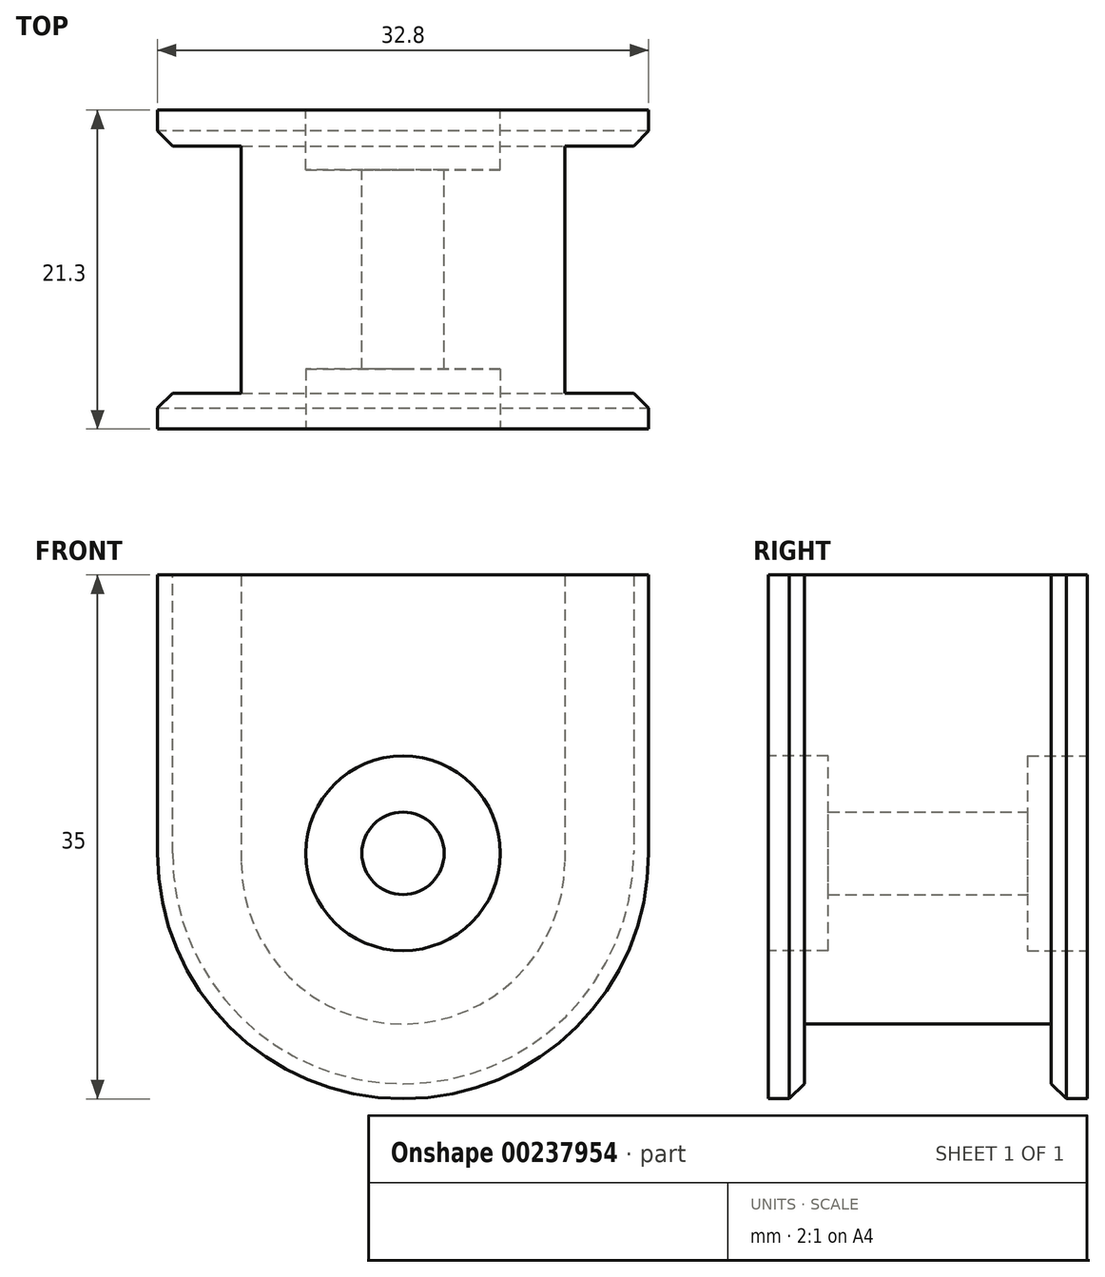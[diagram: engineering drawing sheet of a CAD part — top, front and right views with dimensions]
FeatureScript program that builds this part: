
annotation { "Feature Type Name" : "Feature", "Feature Type Description" : "" }
export const myFeature = defineFeature(function(context is Context, id is Id, definition is map)
    precondition{}
    {
        {
            var Q0;
            Q0=qCreatedBy(makeId("Front.planeOp"),FACE);
            var sketch = newSketch(context, id + "F0", { "sketchPlane" : qUnion([Q0])});
            skLineSegment(sketch, "E0", {"start": v(-10.8, 5) * mm, "end": v(-10.8, -14.2) * mm});
            skLineSegment(sketch, "E1", {"start": v(10.8, 5) * mm, "end": v(10.8, -14.2) * mm});
            skLineSegment(sketch, "E2", {"start": v(-10.8, 5) * mm, "end": v(10.8, 5) * mm});
            skArc(sketch, "E3", {"start": v(-10.8, -14.2) * mm, "mid": v(0, -25) * mm, "end": v(10.8, -14.2) * mm});
            skSolve(sketch);
        }
        {
            var Q0;
            Q0 = qSketchRegion(id + "F0", true);
            extrude(context, id + "F1", {"entities" : qUnion([Q0]), "depth" : 16.5 * mm});
        }
        {
            var Q0;
            Q0=makeQuery(id+"F1.opExtrude","CAP_FACE",FACE,{"disambiguationData":[OSD([sQuery(id+"F0.wireOp",EDGE,"E0"),sQuery(id+"F0.wireOp",EDGE,"E1"),sQuery(id+"F0.wireOp",EDGE,"E2"),sQuery(id+"F0.wireOp",EDGE,"E3")])],"isStart":false});
            var sketch = newSketch(context, id + "F2", { "sketchPlane" : qUnion([Q0])});
            skLineSegment(sketch, "E4.0.0", {"start": v(10.8, -14.2) * mm, "end": v(10.8, 5) * mm});
            skLineSegment(sketch, "E4.0.1", {"start": v(10.8, 5) * mm, "end": v(-10.8, 5) * mm});
            skLineSegment(sketch, "E4.0.2", {"start": v(-10.8, 5) * mm, "end": v(-10.8, -14.2) * mm});
            skArc(sketch, "E4.0.3", {"start": v(-10.8, -14.2) * mm, "mid": v(0, -25) * mm, "end": v(10.8, -14.2) * mm});
            skLineSegment(sketch, "E5.1", {"start": v(16.4, -13.6) * mm, "end": v(16.4, 5) * mm});
            skArc(sketch, "E5.2", {"start": v(-16.4, -13.6) * mm, "mid": v(0, -30) * mm, "end": v(16.4, -13.6) * mm});
            skLineSegment(sketch, "E5.3", {"start": v(-16.4, 5) * mm, "end": v(-16.4, -13.6) * mm});
            skLineSegment(sketch, "E6", {"start": v(-16.4, 5) * mm, "end": v(16.4, 5) * mm});
            skSolve(sketch);
        }
        {
            var Q0;
            Q0=makeQuery(id+"F2.imprint","IMPRINT",FACE,{"disambiguationData":[TD([[makeQuery(id+"F2.imprint","IMPRINT",EDGE,{"derivedFrom":sQuery(id+"F2.wireOp",EDGE,"E4.0.0")}),-1.0]])]});
            var Q1;
            Q1=makeQuery(id+"F2.imprint","IMPRINT",FACE,{"disambiguationData":[TD([[makeQuery(id+"F2.imprint","IMPRINT",EDGE,{"derivedFrom":sQuery(id+"F2.wireOp",EDGE,"E4.0.0")}),1.0]])]});
            extrude(context, id + "F3", {"entities" : qUnion([Q0, Q1]), "operationType" : NewBodyOperationType.ADD, "depth" : 2.4 * mm});
        }
        {
            var Q0;
            Q0=makeQuery(id+"F1.opExtrude","CAP_FACE",FACE,{"disambiguationData":[OSD([sQuery(id+"F0.wireOp",EDGE,"E0"),sQuery(id+"F0.wireOp",EDGE,"E1"),sQuery(id+"F0.wireOp",EDGE,"E2"),sQuery(id+"F0.wireOp",EDGE,"E3")])],"isStart":true});
            var sketch = newSketch(context, id + "F4", { "sketchPlane" : qUnion([Q0])});
            skLineSegment(sketch, "E7.0", {"start": v(-16.4, 5) * mm, "end": v(16.4, 5) * mm});
            skLineSegment(sketch, "E8.0", {"start": v(-16.4, -13.6) * mm, "end": v(-16.4, 5) * mm});
            skArc(sketch, "E9.0", {"start": v(16.4, -13.6) * mm, "mid": v(0, -30) * mm, "end": v(-16.4, -13.6) * mm});
            skLineSegment(sketch, "E10.0", {"start": v(16.4, 5) * mm, "end": v(16.4, -13.6) * mm});
            skSolve(sketch);
        }
        {
            var Q0;
            Q0 = qSketchRegion(id + "F4", true);
            extrude(context, id + "F5", {"entities" : qUnion([Q0]), "operationType" : NewBodyOperationType.ADD, "depth" : 2.4 * mm});
        }
        {
            var Q0;
            Q0=makeQuery(id+"F5.opExtrude","CAP_FACE",FACE,{"disambiguationData":[OSD([sQuery(id+"F4.wireOp",EDGE,"E7.0"),sQuery(id+"F4.wireOp",EDGE,"E8.0"),sQuery(id+"F4.wireOp",EDGE,"E9.0"),sQuery(id+"F4.wireOp",EDGE,"E10.0")])],"isStart":false});
            var sketch = newSketch(context, id + "F6", { "sketchPlane" : qUnion([Q0])});
            skArc(sketch, "E11.0", {"start": v(16.4, -13.6) * mm, "mid": v(0, -30) * mm, "end": v(-16.4, -13.6) * mm, "construction": true});
            skCircle(sketch, "E12", {"center": v(0, -13.6) * mm, "radius": 2.75 * mm});
            skSolve(sketch);
        }
        {
            var Q0;
            Q0 = qSketchRegion(id + "F6", true);
            extrude(context, id + "F7", {"entities" : qUnion([Q0]), "operationType" : NewBodyOperationType.REMOVE, "endBound" : BoundingType.THROUGH_ALL, "oppositeDirection" : true, "depth" : 25 * mm});
        }
        {
            var Q0;
            Q0=makeQuery(id+"F3.opExtrude","CAP_EDGE",EDGE,{"disambiguationData":[OSD([sQuery(id+"F2.wireOp",EDGE,"E5.2")])],"isStart":true});
            var Q1;
            Q1=makeQuery(id+"F5.opExtrude","CAP_EDGE",EDGE,{"disambiguationData":[OSD([sQuery(id+"F4.wireOp",EDGE,"E9.0")])],"isStart":true});
            chamfer(context, id + "F8", {"entities" : qUnion([Q0, Q1]), "width" : 1 * mm, "tangentPropagation" : true});
        }
        {
            var Q0;
            Q0=makeQuery(id+"F5.opExtrude","CAP_FACE",FACE,{"disambiguationData":[OSD([sQuery(id+"F4.wireOp",EDGE,"E7.0"),sQuery(id+"F4.wireOp",EDGE,"E8.0"),sQuery(id+"F4.wireOp",EDGE,"E9.0"),sQuery(id+"F4.wireOp",EDGE,"E10.0")])],"isStart":false});
            var sketch = newSketch(context, id + "F9", { "sketchPlane" : qUnion([Q0])});
            skCircle(sketch, "E13.0", {"center": v(0, -13.6) * mm, "radius": 2.75 * mm, "construction": true});
            skCircle(sketch, "E14", {"center": v(0, -13.6) * mm, "radius": 6.5 * mm});
            skSolve(sketch);
        }
        {
            var Q0;
            Q0 = qSketchRegion(id + "F9", true);
            extrude(context, id + "F10", {"entities" : qUnion([Q0]), "operationType" : NewBodyOperationType.REMOVE, "oppositeDirection" : true, "depth" : 4 * mm});
        }
        {
            var Q0;
            Q0=makeQuery(id+"F3.opExtrude","CAP_FACE",FACE,{"disambiguationData":[OSD([sQuery(id+"F2.wireOp",EDGE,"E5.1"),sQuery(id+"F2.wireOp",EDGE,"E5.2"),sQuery(id+"F2.wireOp",EDGE,"E5.3"),sQuery(id+"F2.wireOp",EDGE,"E6")])],"isStart":false});
            var sketch = newSketch(context, id + "F11", { "sketchPlane" : qUnion([Q0])});
            skCircle(sketch, "E15.0", {"center": v(0, -13.6) * mm, "radius": 2.75 * mm, "construction": true});
            skCircle(sketch, "E16", {"center": v(0, -13.6) * mm, "radius": 6.5 * mm});
            skSolve(sketch);
        }
        {
            var Q0;
            Q0 = qSketchRegion(id + "F11", true);
            extrude(context, id + "F12", {"entities" : qUnion([Q0]), "operationType" : NewBodyOperationType.REMOVE, "oppositeDirection" : true, "depth" : 4 * mm});
        }
    });
